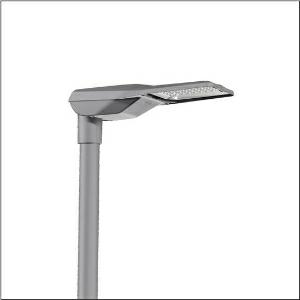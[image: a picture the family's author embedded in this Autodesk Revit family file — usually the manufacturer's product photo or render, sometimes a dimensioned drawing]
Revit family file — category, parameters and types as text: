
# Revit family: streetlight_sl_21_iq_mini___p0_8a_5xe2u31d08jb_69dd
name_source: partatom
category: Lighting Fixtures
units: mm (PartAtom-declared; Revit-internal decimal feet)

## family parameters
Cut with Voids When Loaded = No
Host = Face
Light Source = No
Part Type = Normal
Room Calculation Point = No
Round Connector Dimension = Use Diameter
Shared = No

## types (1)
- --- (1 x LED, 10920 lm, 71.6 W, 3000K)
    Apparent Load = 72 VA
    CIE Flux Codes = 36 69 97 100 100
    Color Rendering = 70
    Color Temperature = 3000K
    Default Elevation = 1800 mm
    Description = Streetlight SL 21 iQ mini, mast luminaire, primary light control with lens, of PMMA, primary optical cover: cover, of toughened safety glass, transparent, light distribution: P0.8a, light emission: direct distribution, primary light characteristic: asymmetric, installation type: post-top, side-entry, LED, High Power LED, rated luminous flux: 10.920lm, luminous efficacy: 153lm/W, light colour: 730, colour temperature: 3000K, control gear: iQ-Comfort, control: pre-setting: linear dimming characteristic, Auto-Match, Temp-Guard, Lumen-Switch, Night-Set, Smart-Wire, Light-Fading, Desk-Remote (wireless, voltage-free reading and setting of iQ features in the workshop via application-optimized NFC function/RFID function), optimised constant luminous flux control (CLO 2.0), mains connection: 220..240V, AC, 50/60Hz, start of lifetime: 72W, end of service life: 75W, reduction: 33W, luminaire housing, of diecast aluminium, powder-coated, Siteco® metallic grey (DB 702S), corrosivity category C5 mid according to DIN EN ISO 12944, please order mast flange separately, inclination adjustable: 0°, 5°, 10°, 15°, sealing non-destructively replaceable, multi-level sealing system, length: 628mm, width: 235mm, height: 110mm, mast flange for spigot size: 42mm (side-entry): 5XC10008XM4, 60/48mm (side-entry/post-top): 5XC10108XM2, 76/60mm (side-entry/post-top): 5XC10108XM1, mounting height: 4..8m, protection rating (complete): IP66, insulation class (complete): insulation class II (safety insulation), certification: CE, ENEC, ENEC+, VDE, impact resistance: IK09, permissible operating ambient temperature for outdoor applications: -40..+50°C, standard-compliant lighting for roads and squares, packaging unit: 1 piece

Light Distribution: P0.8a
    Height = 110 mm
    Lamp = 1 x LED
    Lamp Light Flux = 10920 lm
    Lamp Power = 71.6 W
    Lamp count = 1
    Length = 625 mm
    Luminous efficacy = 153 lm/W
    Manufacturer = Siteco
    ModVariant = No
    Model = 5XE2U31D08JB
    Number of Poles = 1
    OnlyDefault = Yes
    Power Factor = 1
    Product Name = Streetlight SL 21 iQ mini | P0.8a
    Product group = mast luminaire | pylon top
    ProductGroupID = 6100
    Protection Class = Protection class II
    Protection Degree = IP 66
    RLX_Detail_Level = 1
    RLX_Emergency_Light_Flux = 0 lm
    RLX_Emergency_Type = 0
    RLX_Emergency_Type_DB = No
    RlxData = <blob elided: 92209 chars, md5=c1a26b8c>
    Socket = socket
    Standby Power = 0 W
    System Light Flux = 10920 lm
    System Power = 72 W
    Type Comments = factory setting: luminous flux: 100 % | dim-lin: 254 | 746 mA
    Type Image = l_1003519.jpg
    URL = http://relux.com
    VarID = @adj_068602
    Voltage = 0 V
    Weight = 0.00 kg
    Width = 234 mm

## geometry (parser evidence)
native form markers: Blend x4, Sweep x11
no freeform markers — native parametric forms only
